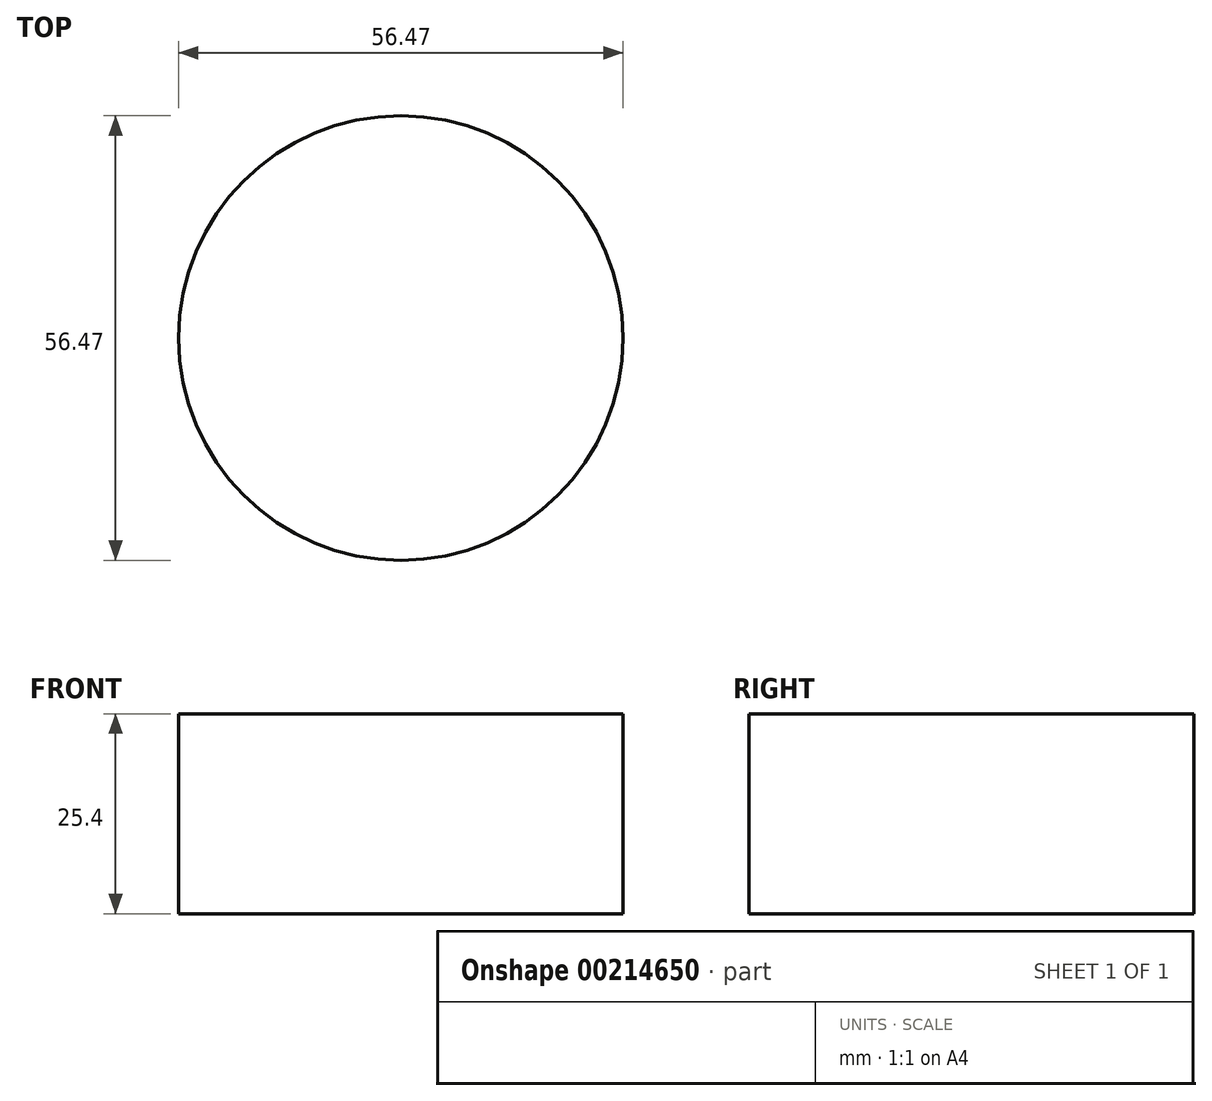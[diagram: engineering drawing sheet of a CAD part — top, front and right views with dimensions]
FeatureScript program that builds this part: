
annotation { "Feature Type Name" : "Feature", "Feature Type Description" : "" }
export const myFeature = defineFeature(function(context is Context, id is Id, definition is map)
    precondition{}
    {
        {
            var Q0;
            Q0=qCreatedBy(makeId("Top.planeOp"),FACE);
            var sketch = newSketch(context, id + "F0", { "sketchPlane" : qUnion([Q0])});
            skLineSegment(sketch, "E0", {"start": v(-67.33, 59.32) * mm, "end": v(-67.33, -61.94) * mm});
            skLineSegment(sketch, "E1", {"start": v(-67.33, -61.94) * mm, "end": v(-12.53, -61.94) * mm});
            skLineSegment(sketch, "E2", {"start": v(-12.53, -61.94) * mm, "end": v(-12.53, 59.6) * mm});
            skLineSegment(sketch, "E3", {"start": v(-12.82, 59.6) * mm, "end": v(-67.33, 59.32) * mm});
            skLineSegment(sketch, "E4", {"start": v(7.29, 0) * mm, "end": v(59.46, 0) * mm});
            skLineSegment(sketch, "E5", {"start": v(59.46, 0) * mm, "end": v(59.46, -61.94) * mm});
            skLineSegment(sketch, "E6", {"start": v(7.29, 0) * mm, "end": v(7.29, -61.94) * mm});
            skLineSegment(sketch, "E7", {"start": v(7.29, -61.94) * mm, "end": v(59.46, -61.94) * mm});
            skCircle(sketch, "E8", {"center": v(32.65, 35.41) * mm, "radius": 28.24 * mm});
            skSolve(sketch);
        }
        {
            var Q0;
            Q0=makeQuery(id+"F0.imprint","IMPRINT",FACE,{"disambiguationData":[TD([[makeQuery(id+"F0.imprint","IMPRINT",EDGE,{"derivedFrom":sQuery(id+"F0.wireOp",EDGE,"E8")}),1.0]])]});
            extrude(context, id + "F1", {"entities" : qUnion([Q0]), "depth" : 25.4 * mm});
        }
    });
